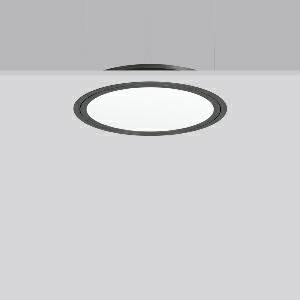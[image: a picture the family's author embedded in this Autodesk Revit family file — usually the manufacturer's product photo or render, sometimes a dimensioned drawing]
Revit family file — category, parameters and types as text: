
# Revit family: triona_round_e_312419_0031_12_726e
name_source: partatom
category: Lighting Fixtures
units: mm (PartAtom-declared; Revit-internal decimal feet)

## family parameters
Cut with Voids When Loaded = No
Host = Face
Light Source = No
Part Type = Normal
Room Calculation Point = No
Round Connector Dimension = Use Diameter
Shared = No

## types (1)
- TRIONA round E (1 x LED Modul 830, 4650 lm, 3000)
    Apparent Load = 48 VA
    CIE Flux Codes = 49 80 96 100 100
    Color Rendering = 80
    Color Temperature = 3000
    Default Elevation = 1800 mm
    Description = Series: TRIONA round
Decorative round LED recessed surface luminaire. Cover made of sheet steel, powder-coated. Frame made of aluminium, powder-coated. Recessed ring: aluminium extrusion profile, powder coated. Light emission through a diffuser: plastic, opal. Lightguide and diffuser made of non-yellowing plastic (PMMA). Lateral light emission (RZB SIDELITE technology) for above-average homogeneous light distribution. Suitable for installation in cavity ceilings. Tool-free mounting system thanks to the rocker arm mechanism (patent pending). Electronic ballast included. Very easy installation thanks to Plug+Play connection. 
Colour: anthracite metallic (DB703)
Diameter: 505 mm
Height: 2 mm
Cut-out diameter: 482 mm
Recess height: 100 mm
Luminaire: recess height: 89 mm
Lamp: LED
Socket: without socket
Colour temperature: 3000K
Colour rendering index (CRI): 80
System power: 48 W
Rated luminous flux: 4650 lm
Luminous efficiency: 97 lm/W
Control gear: Converter, dimmable, DALI
Protection class: I
Type of protection: IP 40
    Height = 0 mm  [stored 0 ft]
    Lamp = 1 x LED Modul 830
    Lamp Light Flux = 4650 lm
    Lamp count = 1
    Length = 505 mm
    Lifetime = 50000 h
    Luminous efficacy = 97 lm/W
    Manufacturer = RZB
    ModVariant = No
    Model = 312419.0031.12
    Mounting Place = Ceiling
    Mounting Type = Recessed
    Number of Poles = 1
    OnlyDefault = Yes
    Power Factor = 1
    Product Name = TRIONA round E
    Product group = Recessed modular luminaires
    ProductGroupID = 406
    Protection Class = Protection class I
    Protection Degree = IP 20
    RLX_Detail_Level = 1
    RLX_Emergency_Light_Flux = 0 lm
    RLX_Emergency_Type = 0
    RLX_Emergency_Type_DB = No
    RlxData = <blob elided: 33261 chars, md5=901347c0>
    Socket = socket
    Standby Power = 0 W
    System Light Flux = 4650 lm
    System Power = 48 W
    Type Comments = Product without accessories
    Type Image = 312419.0031.12.jpg
    URL = http://relux.com
    VarID = ---
    Voltage = 230 V
    Voltage Range = 220-240 V
    Weight = 0.00 kg
    Width = 0 mm  [stored 0 ft]

note: [stored X ft] marks values corroborated as IEEE doubles in the binary element streams (Revit-internal decimal feet)

## geometry (parser evidence)
native form markers: Blend x4, Sweep x8
no freeform markers — native parametric forms only
